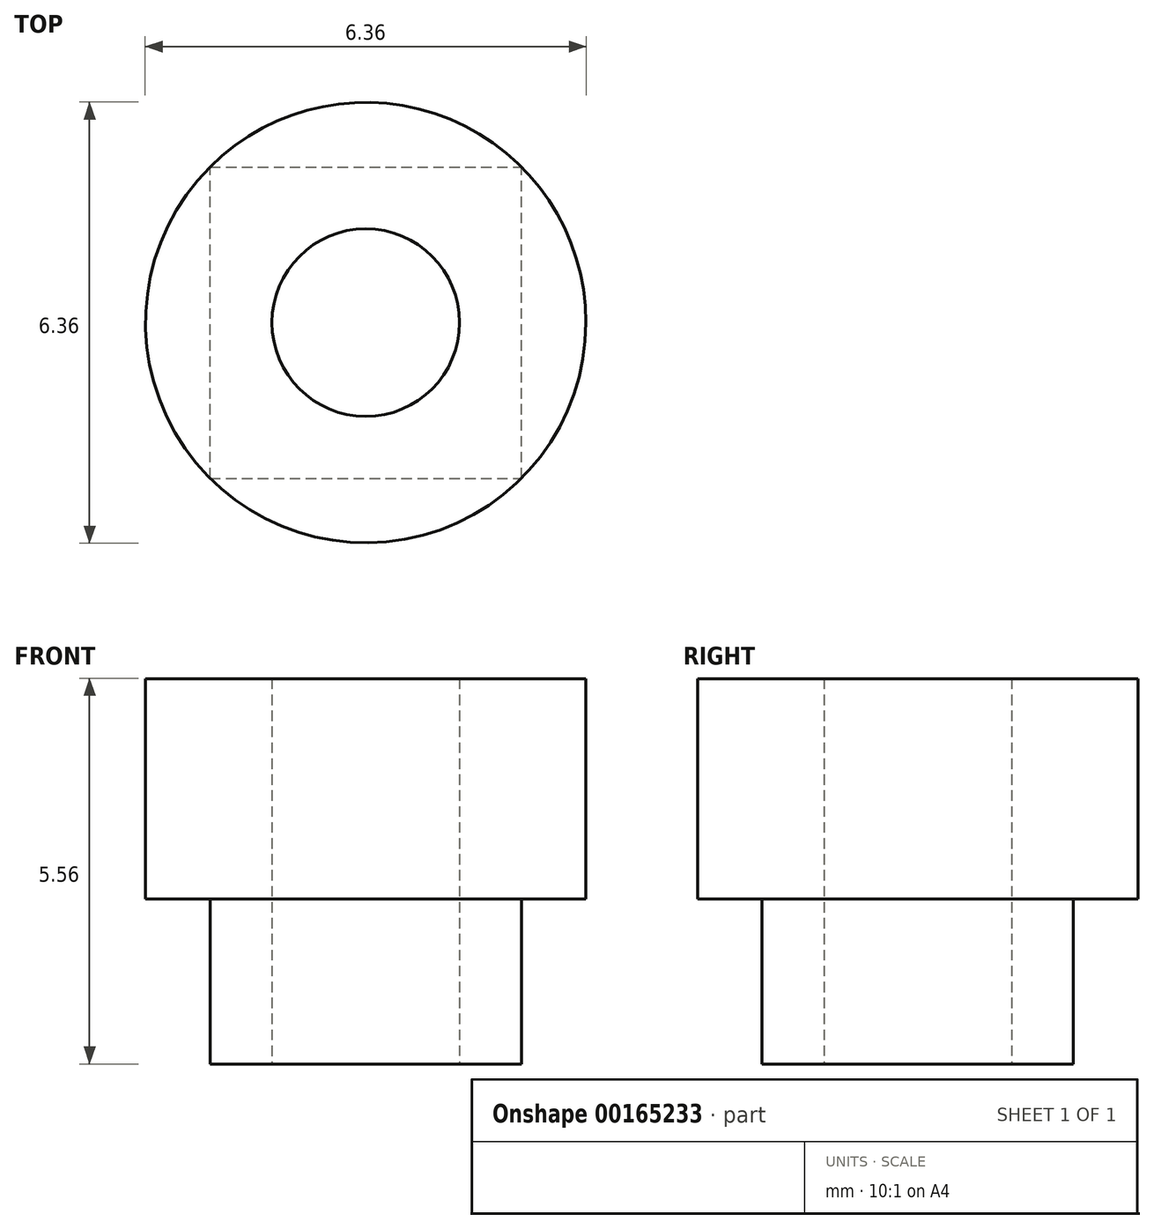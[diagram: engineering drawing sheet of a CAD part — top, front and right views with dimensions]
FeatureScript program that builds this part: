
annotation { "Feature Type Name" : "Feature", "Feature Type Description" : "" }
export const myFeature = defineFeature(function(context is Context, id is Id, definition is map)
    precondition{}
    {
        {
            var Q0;
            Q0=qCreatedBy(makeId("Top.planeOp"),FACE);
            var sketch = newSketch(context, id + "F0", { "sketchPlane" : qUnion([Q0])});
            skCircle(sketch, "E0", {"center": v(0, 0) * mm, "radius": 3.18 * mm});
            skSolve(sketch);
        }
        {
            var Q0;
            Q0=qSketchRegion(id+"F0",true);
            extrude(context, id + "F1", {"entities" : qUnion([Q0]), "depth" : 3.17 * mm});
        }
        {
            var Q0;
            Q0=makeQuery(id+"F1.opExtrude","CAP_FACE",FACE,{"disambiguationData":[OSD([sQuery(id+"F0.wireOp",EDGE,"E0")])],"isStart":true});
            var sketch = newSketch(context, id + "F2", { "sketchPlane" : qUnion([Q0])});
            skLineSegment(sketch, "E1.bottom", {"start": v(-2.25, 2.25) * mm, "end": v(2.25, 2.25) * mm});
            skLineSegment(sketch, "E1.top", {"start": v(-2.25, -2.25) * mm, "end": v(2.25, -2.25) * mm});
            skLineSegment(sketch, "E1.left", {"start": v(-2.25, 2.25) * mm, "end": v(-2.25, -2.25) * mm});
            skLineSegment(sketch, "E1.right", {"start": v(2.25, 2.25) * mm, "end": v(2.25, -2.25) * mm});
            skPoint(sketch, "E1.middle", {"position": v(0, 0) * mm});
            skSolve(sketch);
        }
        {
            var Q0;
            Q0 = qSketchRegion(id + "F2", true);
            extrude(context, id + "F3", {"entities" : qUnion([Q0]), "operationType" : NewBodyOperationType.ADD, "depth" : 2.38 * mm});
        }
        {
            var Q0;
            Q0=makeQuery(id+"F3.opExtrude","CAP_FACE",FACE,{"disambiguationData":[OSD([sQuery(id+"F2.wireOp",EDGE,"E1.bottom"),sQuery(id+"F2.wireOp",EDGE,"E1.top"),sQuery(id+"F2.wireOp",EDGE,"E1.left"),sQuery(id+"F2.wireOp",EDGE,"E1.right")])],"isStart":false});
            var sketch = newSketch(context, id + "F4", { "sketchPlane" : qUnion([Q0])});
            skCircle(sketch, "E2", {"center": v(0, 0) * mm, "radius": 1.35 * mm});
            skSolve(sketch);
        }
        {
            var Q0;
            Q0 = qSketchRegion(id + "F4", true);
            extrude(context, id + "F5", {"entities" : qUnion([Q0]), "operationType" : NewBodyOperationType.REMOVE, "oppositeDirection" : true, "depth" : 6.35 * mm});
        }
    });
